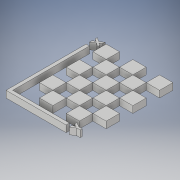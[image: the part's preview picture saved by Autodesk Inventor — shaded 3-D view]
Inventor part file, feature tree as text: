
AUTODESK INVENTOR PART (.ipt)
format: ipt  version: 2019 (Build 230136000, 136)  size: 271,872 bytes
history: native  units: in
note: dims shown in document units (in); Inventor stores cm internally (conversion verified against a paired STEP export)
features: extrude x5, sketch x5
ambient origin geometry x8: Origin, YZ Plane, XZ Plane, XY Plane, X Axis, Y Axis, Z Axis, Center Point
bodies: Solid1 (feature_tree)
feature tree (10):
  extrude  "Extrusion1"  Depth=6.2992in
  extrude  "Extrusion2"  Depth=3.1496in
  sketch  "Sketch3"  dims[d6=0.7874in d7=0.0in d8=3.937in]
  extrude  "Extrusion5"  Depth=3.937in
  extrude  "Extrusion4"  Depth=0.3937in TaperAngle=0.0deg
  extrude  "Extrusion6"  Depth=0.7874in
  sketch  "Sketch1"  dims[d0=5.5118in d1=6.2992in]
  sketch  "Sketch2"  dims[d4=2.7559in d5=3.1496in]
  sketch  "Sketch4"  dims[d9=4.7244in d10=0.3937in d11=0.0in]
  sketch  "Sketch5"  dims[d12=0.7874in d13=0.7874in d14=0.7874in d15=0.7874in d16=0.7874in d17=0.7874in d18=0.7874in d19=0.7874in d20=0.7874in d21=0.7874in d22=0.7874in d23=0.7874in d25=0.7874in d26=0.7874in d27=0.7874in d28=0.7874in d29=0.7874in d30=0.7874in d31=0.7874in d32=0.7874in d33=0.7874in d34=0.7874in d35=0.7874in d36=0.7874in d37=0.7874in d38=0.7874in d39=0.7874in d40=0.7874in d41=0.7874in d42=0.7874in d43=0.7874in d44=0.7874in d45=0.7874in d46=0.7874in d47=0.7874in d48=0.7874in d49=0.7874in d50=0.7874in d53=0.1969in d54=0.1969in d55=0.1969in d56=0.1969in d57=4.7244in d58=3.5433in d63=0.4823in d73=0.1969in d75=0.3937in d76=0.0in d77=0.7874in d78=0.7874in d79=0.7874in d80=0.7874in d81=0.7874in d82=0.7874in d83=0.7874in d84=0.7874in d85=0.7874in d86=0.3937in d87=0.0in d88=0.1969in d90=0.1969in d91=0.7874in d92=0.0in]
